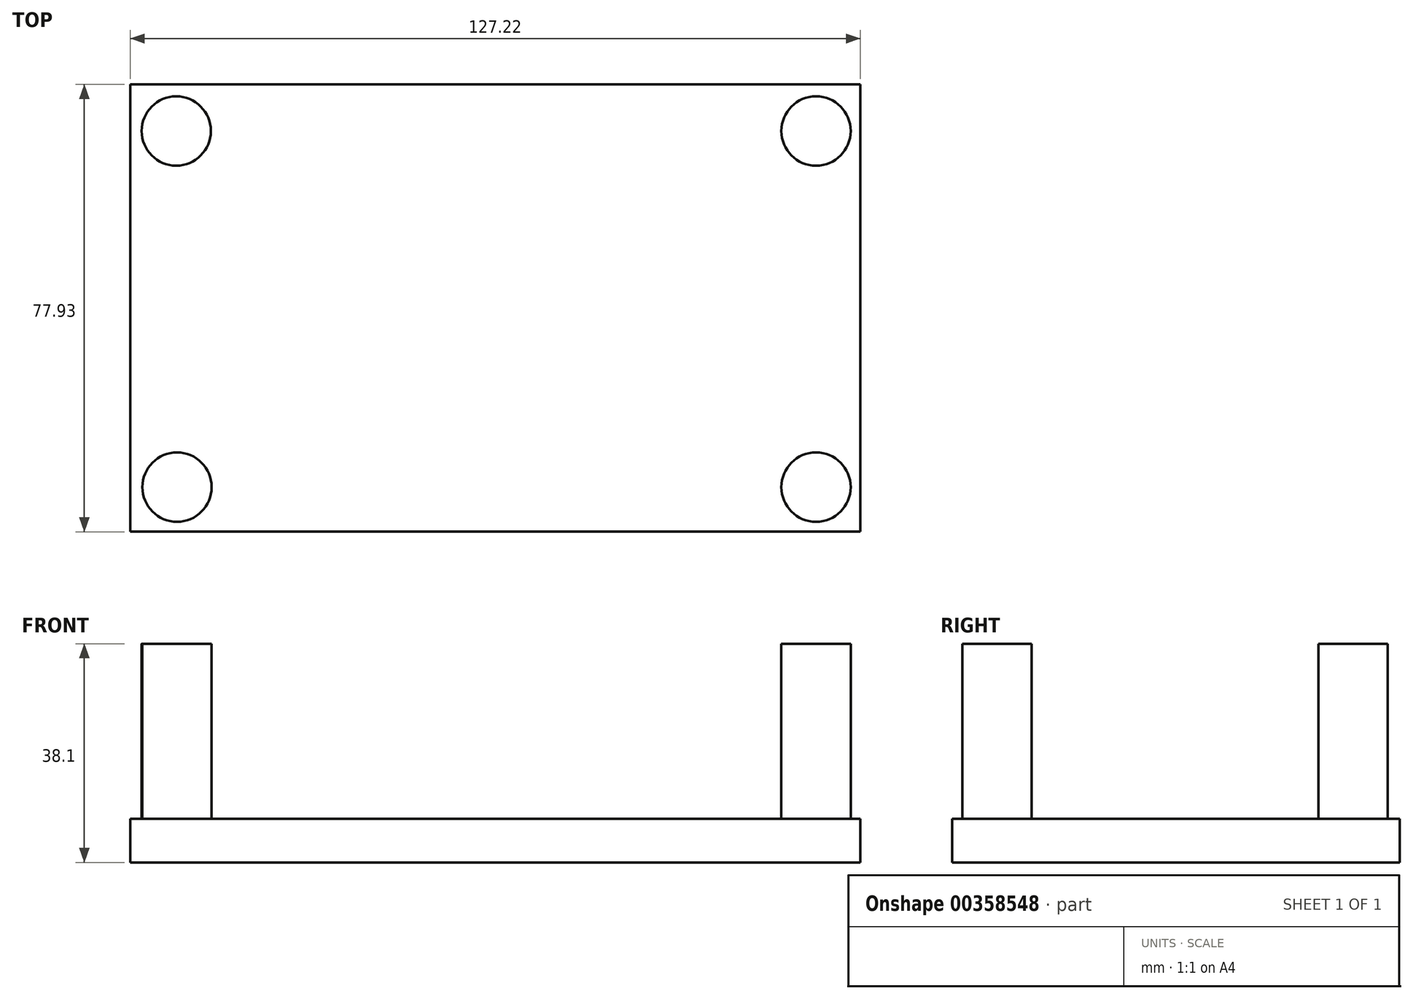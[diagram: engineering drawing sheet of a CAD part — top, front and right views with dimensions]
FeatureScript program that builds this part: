
annotation { "Feature Type Name" : "Feature", "Feature Type Description" : "" }
export const myFeature = defineFeature(function(context is Context, id is Id, definition is map)
    precondition{}
    {
        {
            var Q0;
            Q0=qCreatedBy(makeId("Top.planeOp"),FACE);
            var sketch = newSketch(context, id + "F0", { "sketchPlane" : qUnion([Q0])});
            skLineSegment(sketch, "E0.bottom", {"start": v(-55.17, 29.2) * mm, "end": v(72.05, 29.2) * mm});
            skLineSegment(sketch, "E0.top", {"start": v(-55.17, -48.73) * mm, "end": v(72.05, -48.73) * mm});
            skLineSegment(sketch, "E0.left", {"start": v(-55.17, 29.2) * mm, "end": v(-55.17, -48.73) * mm});
            skLineSegment(sketch, "E0.right", {"start": v(72.05, 29.2) * mm, "end": v(72.05, -48.73) * mm});
            skSolve(sketch);
        }
        {
            var Q0;
            Q0 = qSketchRegion(id + "F0", true);
            extrude(context, id + "F1", {"entities" : qUnion([Q0]), "depth" : 7.62 * mm});
        }
        {
            var Q0;
            Q0=qCreatedBy(makeId("Top.planeOp"),FACE);
            var sketch = newSketch(context, id + "F2", { "sketchPlane" : qUnion([Q0])});
            skCircle(sketch, "E1", {"center": v(-47.02, -40.95) * mm, "radius": 6.03 * mm});
            skCircle(sketch, "E2", {"center": v(-47.16, 21.09) * mm, "radius": 6.03 * mm});
            skCircle(sketch, "E3", {"center": v(64.3, -40.95) * mm, "radius": 6.03 * mm});
            skCircle(sketch, "E4", {"center": v(64.3, 21.09) * mm, "radius": 6.03 * mm});
            skSolve(sketch);
        }
        {
            var Q0;
            Q0 = qSketchRegion(id + "F2", true);
            extrude(context, id + "F3", {"entities" : qUnion([Q0]), "operationType" : NewBodyOperationType.ADD, "depth" : 38.1 * mm});
        }
    });
